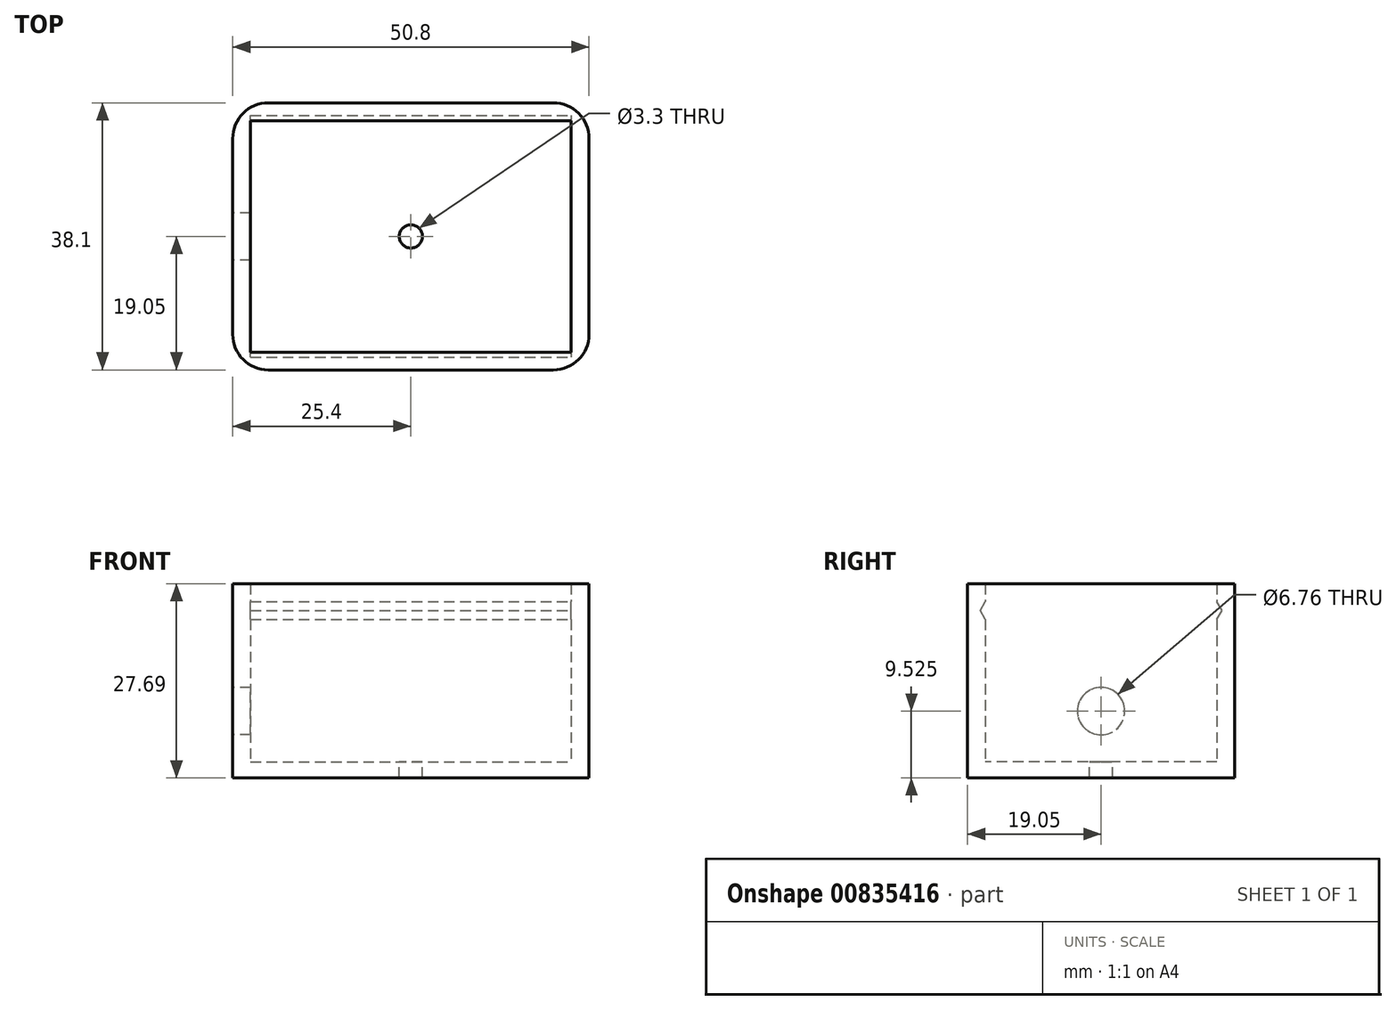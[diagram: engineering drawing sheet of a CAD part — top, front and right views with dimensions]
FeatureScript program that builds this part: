
annotation { "Feature Type Name" : "Feature", "Feature Type Description" : "" }
export const myFeature = defineFeature(function(context is Context, id is Id, definition is map)
    precondition{}
    {
        {
            var Q0;
            Q0=qCreatedBy(makeId("Top.planeOp"),FACE);
            var sketch = newSketch(context, id + "F0", { "sketchPlane" : qUnion([Q0])});
            skLineSegment(sketch, "E0.bottom", {"start": v(0, 0) * mm, "end": v(50.8, 0) * mm});
            skLineSegment(sketch, "E0.top", {"start": v(0, 38.1) * mm, "end": v(50.8, 38.1) * mm});
            skLineSegment(sketch, "E0.left", {"start": v(0, 0) * mm, "end": v(0, 38.1) * mm});
            skLineSegment(sketch, "E0.right", {"start": v(50.8, 0) * mm, "end": v(50.8, 38.1) * mm});
            skSolve(sketch);
        }
        {
            var Q0;
            Q0=makeQuery(id+"F0.imprint","IMPRINT",FACE,{"disambiguationData":[TD([[makeQuery(id+"F0.imprint","IMPRINT",EDGE,{"derivedFrom":sQuery(id+"F0.wireOp",EDGE,"E0.bottom")}),1.0]])]});
            extrude(context, id + "F1", {"entities" : qUnion([Q0]), "depth" : 2.3 * mm, "offsetDistance" : 25.4 * mm});
        }
        {
            var Q0;
            Q0=makeQuery(id+"F1.opExtrude","CAP_FACE",FACE,{"disambiguationData":[OSD([sQuery(id+"F0.wireOp",EDGE,"E0.bottom"),sQuery(id+"F0.wireOp",EDGE,"E0.top"),sQuery(id+"F0.wireOp",EDGE,"E0.left"),sQuery(id+"F0.wireOp",EDGE,"E0.right")])],"isStart":false});
            var sketch = newSketch(context, id + "F2", { "sketchPlane" : qUnion([Q0])});
            skLineSegment(sketch, "E1.bottom", {"start": v(0, 38.1) * mm, "end": v(50.8, 38.1) * mm});
            skLineSegment(sketch, "E1.top", {"start": v(0, 0) * mm, "end": v(50.8, 0) * mm});
            skLineSegment(sketch, "E1.left", {"start": v(0, 38.1) * mm, "end": v(0, 0) * mm});
            skLineSegment(sketch, "E1.right", {"start": v(50.8, 38.1) * mm, "end": v(50.8, 0) * mm});
            skLineSegment(sketch, "E2.0", {"start": v(2.54, 35.56) * mm, "end": v(48.26, 35.56) * mm});
            skLineSegment(sketch, "E2.1", {"start": v(2.54, 35.56) * mm, "end": v(2.54, 2.54) * mm});
            skLineSegment(sketch, "E2.2", {"start": v(2.54, 2.54) * mm, "end": v(48.26, 2.54) * mm});
            skLineSegment(sketch, "E2.3", {"start": v(48.26, 35.56) * mm, "end": v(48.26, 2.54) * mm});
            skSolve(sketch);
        }
        {
            var Q0;
            Q0 = qSketchRegion(id + "F2", true);
            extrude(context, id + "F3", {"entities" : qUnion([Q0]), "operationType" : NewBodyOperationType.ADD, "depth" : 25.4 * mm, "offsetDistance" : 25.4 * mm});
        }
        {
            var Q0;
            Q0=makeQuery(id+"F3.opExtrude","SWEPT_FACE",FACE,{"disambiguationData":[OSD([sQuery(id+"F2.wireOp",EDGE,"E2.1")])]});
            cPlane(context, id + "F4", {"entities" : qUnion([Q0]), "cplaneType" : CPlaneType.OFFSET, "offset" : 12.7 * mm, "width" : 152.4 * mm, "height" : 152.4 * mm});
        }
        {
            var Q0;
            Q0=qCreatedBy(id+"F4.planeOp",FACE);
            var sketch = newSketch(context, id + "F5", { "sketchPlane" : qUnion([Q0])});
            skLineSegment(sketch, "E3", {"start": v(2.54, 30.25) * mm, "end": v(2.54, 0) * mm, "construction": true});
            skLineSegment(sketch, "E4", {"start": v(35.56, 27.73) * mm, "end": v(35.56, 0) * mm, "construction": true});
            skLineSegment(sketch, "E5", {"start": v(2.54, 25.15) * mm, "end": v(1.8, 23.88) * mm});
            skLineSegment(sketch, "E6", {"start": v(1.8, 23.88) * mm, "end": v(2.54, 22.6) * mm});
            skLineSegment(sketch, "E7", {"start": v(2.54, 22.6) * mm, "end": v(2.54, 25.15) * mm});
            skLineSegment(sketch, "E8", {"start": v(35.56, 25.15) * mm, "end": v(36.3, 23.88) * mm});
            skLineSegment(sketch, "E9", {"start": v(36.3, 23.88) * mm, "end": v(35.56, 22.6) * mm});
            skLineSegment(sketch, "E10", {"start": v(35.56, 25.15) * mm, "end": v(35.56, 22.6) * mm});
            skSolve(sketch);
        }
        {
            var Q0;
            Q0 = qSketchRegion(id + "F5", true);
            var Q1;
            Q1=makeQuery(id+"F3.opExtrude","SWEPT_FACE",FACE,{"disambiguationData":[OSD([sQuery(id+"F2.wireOp",EDGE,"E2.1")])]});
            var Q2;
            Q2=makeQuery(id+"F3.opExtrude","SWEPT_FACE",FACE,{"disambiguationData":[OSD([sQuery(id+"F2.wireOp",EDGE,"E2.3")])]});
            extrude(context, id + "F6", {"entities" : qUnion([Q0]), "operationType" : NewBodyOperationType.REMOVE, "endBound" : BoundingType.UP_TO_SURFACE, "oppositeDirection" : true, "depth" : 25.4 * mm, "endBoundEntityFace" : qUnion([Q1]), "offsetDistance" : 25.4 * mm, "hasSecondDirection" : true, "secondDirectionBound" : SecondDirectionBoundingType.UP_TO_SURFACE, "secondDirectionOppositeDirection" : false, "secondDirectionDepth" : 25.4 * mm, "secondDirectionBoundEntityFace" : qUnion([Q2])});
        }
        {
            var Q0;
            Q0=makeQuery(id+"F1.opExtrude","CAP_FACE",FACE,{"disambiguationData":[OSD([sQuery(id+"F0.wireOp",EDGE,"E0.bottom"),sQuery(id+"F0.wireOp",EDGE,"E0.top"),sQuery(id+"F0.wireOp",EDGE,"E0.left"),sQuery(id+"F0.wireOp",EDGE,"E0.right")])],"isStart":false});
            var sketch = newSketch(context, id + "F7", { "sketchPlane" : qUnion([Q0])});
            skPoint(sketch, "E11", {"position": v(25.4, 19.05) * mm});
            skPoint(sketch, "E11.positionSnap0", {"position": v(25.4, 35.56) * mm});
            skPoint(sketch, "E11.positionSnap1", {"position": v(2.54, 19.05) * mm});
            skSolve(sketch);
        }
        {
            var Q0;
            Q0=sQuery(id+"F7.wireOp",VERTEX,"E11");
            var Q1;
            Q1=makeQuery(id+"F1.opExtrude","SWEPT_BODY",BODY,{"disambiguationData":[OSD([sQuery(id+"F0.wireOp",EDGE,"E0.bottom"),sQuery(id+"F0.wireOp",EDGE,"E0.top"),sQuery(id+"F0.wireOp",EDGE,"E0.left"),sQuery(id+"F0.wireOp",EDGE,"E0.right")])]});
            hole(context, id + "F8", {"style" : HoleStyle.SIMPLE, "endStyle" : HoleEndStyle.THROUGH, "standardTappedOrClearance" : lookupTablePath({ "fit" : "Normal", "standard" : "ISO", "size" : "M3", "type" : "Clearance" }), "standardBlindInLast" : lookupTablePath({ "fit" : "Standard", "standard" : "ISO", "size" : "M3", "type" : "Clearance" }), "holeDiameter" : 3.3 * mm, "majorDiameter" : 6.35 * mm, "isTappedThrough" : true, "tappedDepth" : 12.7 * mm, "tapClearance" : 3, "startFromSketch" : true, "locations" : qUnion([Q0]), "scope" : qUnion([Q1])});
        }
        {
            var Q0;
            Q0=makeQuery(id+"F3.boolean.opBoolean","MERGE",FACE,{"derivedFrom":[makeQuery(id+"F1.opExtrude","SWEPT_FACE",FACE,{"disambiguationData":[OSD([sQuery(id+"F0.wireOp",EDGE,"E0.left")])]}),makeQuery(id+"F3.opExtrude","SWEPT_FACE",FACE,{"disambiguationData":[OSD([sQuery(id+"F2.wireOp",EDGE,"E1.left")])]})]});
            var sketch = newSketch(context, id + "F9", { "sketchPlane" : qUnion([Q0])});
            skPoint(sketch, "E12", {"position": v(-19.05, 9.53) * mm});
            skPoint(sketch, "E12.positionSnap0", {"position": v(-19.05, 0) * mm});
            skSolve(sketch);
        }
        {
            var Q0;
            Q0=sQuery(id+"F9.wireOp",VERTEX,"E12");
            var Q1;
            Q1=makeQuery(id+"F1.opExtrude","SWEPT_BODY",BODY,{"disambiguationData":[OSD([sQuery(id+"F0.wireOp",EDGE,"E0.bottom"),sQuery(id+"F0.wireOp",EDGE,"E0.top"),sQuery(id+"F0.wireOp",EDGE,"E0.left"),sQuery(id+"F0.wireOp",EDGE,"E0.right")])]});
            hole(context, id + "F10", {"style" : HoleStyle.SIMPLE, "endStyle" : HoleEndStyle.BLIND, "standardTappedOrClearance" : lookupTablePath({ "fit" : "Normal (ASME)", "standard" : "ANSI", "size" : "1/4", "type" : "Clearance" }), "standardBlindInLast" : lookupTablePath({ "fit" : "Free", "standard" : "ANSI", "size" : "1/4", "type" : "Clearance" }), "holeDiameter" : 6.76 * mm, "majorDiameter" : 6.35 * mm, "holeDepth" : 38.1 * mm, "isTappedThrough" : true, "tappedDepth" : 12.7 * mm, "tapClearance" : 3, "startFromSketch" : true, "locations" : qUnion([Q0]), "scope" : qUnion([Q1])});
        }
        {
            var Q0;
            Q0=makeQuery(id+"F3.boolean.opBoolean","MERGE",EDGE,{"derivedFrom":[makeQuery(id+"F1.opExtrude","SWEPT_EDGE",EDGE,{"disambiguationData":[OSD([sQuery(id+"F0.wireOp",EDGE,"E0.bottom"),sQuery(id+"F0.wireOp",EDGE,"E0.left")])]}),makeQuery(id+"F3.opExtrude","SWEPT_EDGE",EDGE,{"disambiguationData":[OSD([sQuery(id+"F2.wireOp",EDGE,"E1.top"),sQuery(id+"F2.wireOp",EDGE,"E1.left")])]})]});
            var Q1;
            Q1=makeQuery(id+"F3.boolean.opBoolean","MERGE",EDGE,{"derivedFrom":[makeQuery(id+"F1.opExtrude","SWEPT_EDGE",EDGE,{"disambiguationData":[OSD([sQuery(id+"F0.wireOp",EDGE,"E0.bottom"),sQuery(id+"F0.wireOp",EDGE,"E0.right")])]}),makeQuery(id+"F3.opExtrude","SWEPT_EDGE",EDGE,{"disambiguationData":[OSD([sQuery(id+"F2.wireOp",EDGE,"E1.top"),sQuery(id+"F2.wireOp",EDGE,"E1.right")])]})]});
            var Q2;
            Q2=makeQuery(id+"F3.boolean.opBoolean","MERGE",EDGE,{"derivedFrom":[makeQuery(id+"F1.opExtrude","SWEPT_EDGE",EDGE,{"disambiguationData":[OSD([sQuery(id+"F0.wireOp",EDGE,"E0.top"),sQuery(id+"F0.wireOp",EDGE,"E0.right")])]}),makeQuery(id+"F3.opExtrude","SWEPT_EDGE",EDGE,{"disambiguationData":[OSD([sQuery(id+"F2.wireOp",EDGE,"E1.bottom"),sQuery(id+"F2.wireOp",EDGE,"E1.right")])]})]});
            var Q3;
            Q3=makeQuery(id+"F3.boolean.opBoolean","MERGE",EDGE,{"derivedFrom":[makeQuery(id+"F1.opExtrude","SWEPT_EDGE",EDGE,{"disambiguationData":[OSD([sQuery(id+"F0.wireOp",EDGE,"E0.top"),sQuery(id+"F0.wireOp",EDGE,"E0.left")])]}),makeQuery(id+"F3.opExtrude","SWEPT_EDGE",EDGE,{"disambiguationData":[OSD([sQuery(id+"F2.wireOp",EDGE,"E1.bottom"),sQuery(id+"F2.wireOp",EDGE,"E1.left")])]})]});
            fillet(context, id + "F11", {"entities" : qUnion([Q0, Q1, Q2, Q3]), "radius" : 5.08 * mm, "tangentPropagation" : true, "allowEdgeOverflow" : false});
        }
    });
